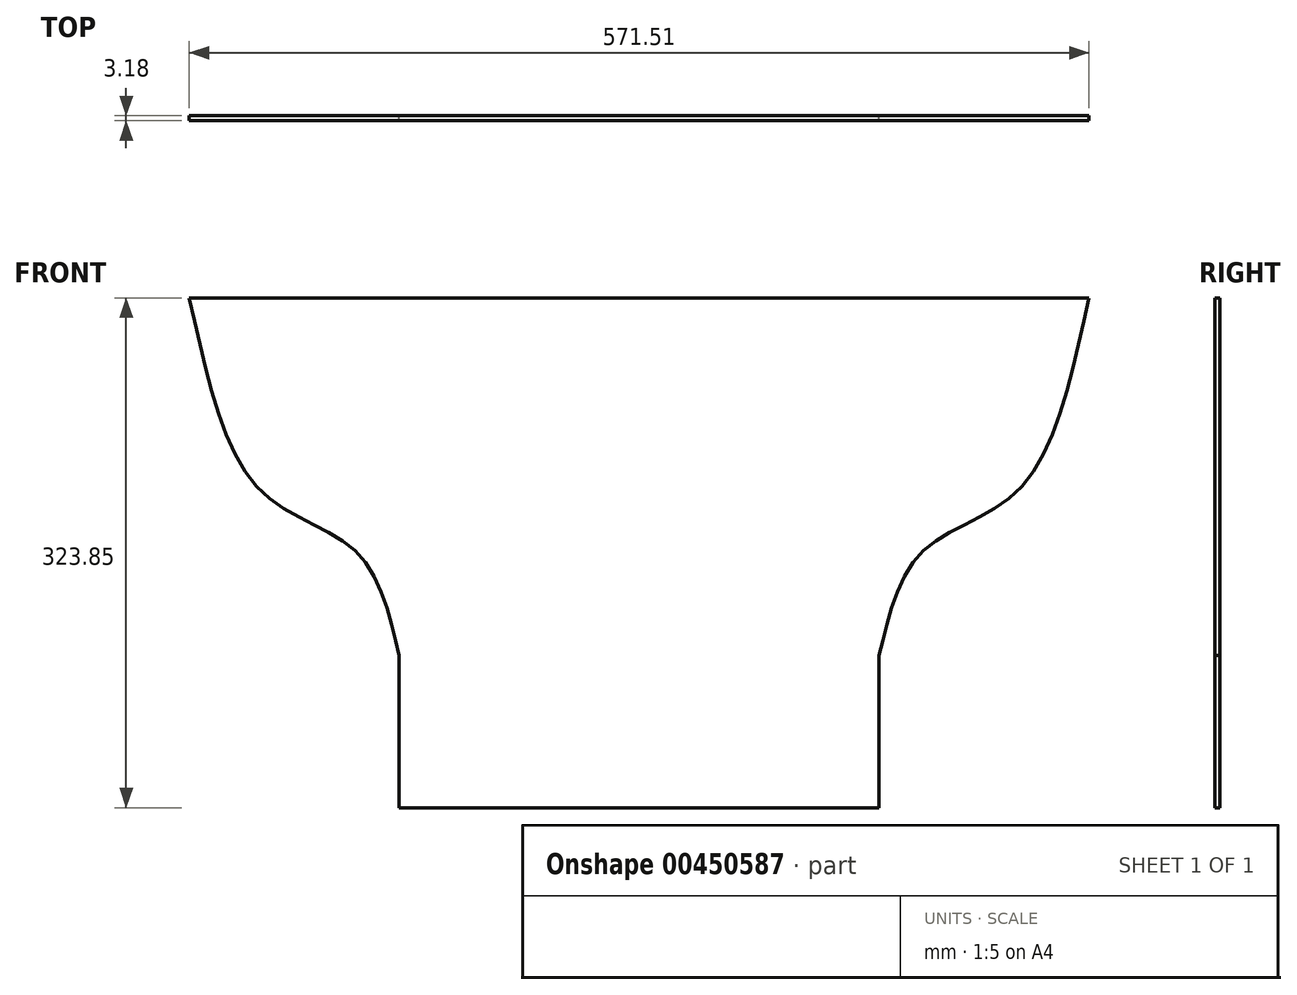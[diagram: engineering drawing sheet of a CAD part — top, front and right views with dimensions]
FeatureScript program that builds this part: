
annotation { "Feature Type Name" : "Feature", "Feature Type Description" : "" }
export const myFeature = defineFeature(function(context is Context, id is Id, definition is map)
    precondition{}
    {
        {
            var Q0;
            Q0=qCreatedBy(makeId("Front.planeOp"),FACE);
            var sketch = newSketch(context, id + "F0", { "sketchPlane" : qUnion([Q0])});
            skLineSegment(sketch, "E0.bottom", {"start": v(282.58, -129) * mm, "end": v(-288.93, -129) * mm, "construction": true});
            skLineSegment(sketch, "E0.top", {"start": v(282.58, 194.84) * mm, "end": v(-288.93, 194.84) * mm, "construction": true});
            skLineSegment(sketch, "E0.left", {"start": v(282.58, -129) * mm, "end": v(282.58, 194.84) * mm, "construction": true});
            skLineSegment(sketch, "E0.right", {"start": v(-288.93, -129) * mm, "end": v(-288.93, 194.84) * mm, "construction": true});
            skPoint(sketch, "E0.middle", {"position": v(-3.17, 32.92) * mm});
            skPoint(sketch, "E1", {"position": v(149.23, -129) * mm});
            skPoint(sketch, "E2", {"position": v(-155.57, -129) * mm});
            skFitSpline(sketch, "E3", {"points": [v(-288.93, 194.84) * mm, v(-244.59, 73.28) * mm, v(-182.17, 32.92) * mm, v(-155.57, -32.33) * mm], "startDerivative": vector(77.13, -333.51) * mm, "endDerivative": vector(50.5, -211.24) * mm});
            skLineSegment(sketch, "E4", {"start": v(-3.17, 194.84) * mm, "end": v(-3.17, -129) * mm, "construction": true});
            skFitSpline(sketch, "E5.MirrorCS", {"points": [v(282.58, 194.84) * mm, v(238.24, 73.28) * mm, v(175.82, 32.92) * mm, v(149.23, -32.33) * mm], "startDerivative": vector(-77.13, -333.51) * mm, "endDerivative": vector(-50.5, -211.24) * mm});
            skLineSegment(sketch, "E6", {"start": v(149.23, -129) * mm, "end": v(-155.57, -129) * mm});
            skLineSegment(sketch, "E7", {"start": v(282.58, 194.84) * mm, "end": v(-288.93, 194.84) * mm});
            skLineSegment(sketch, "E8", {"start": v(-155.57, -32.33) * mm, "end": v(-155.57, -129) * mm});
            skLineSegment(sketch, "E9", {"start": v(149.23, -32.33) * mm, "end": v(149.23, -129) * mm});
            skSolve(sketch);
        }
        {
            var Q0;
            Q0=makeQuery(id+"F0.imprint","IMPRINT",FACE,{"disambiguationData":[TD([[makeQuery(id+"F0.imprint","IMPRINT",EDGE,{"derivedFrom":sQuery(id+"F0.wireOp",EDGE,"E3")}),1.0]])]});
            extrude(context, id + "F1", {"entities" : qUnion([Q0]), "depth" : 3.17 * mm});
        }
    });
